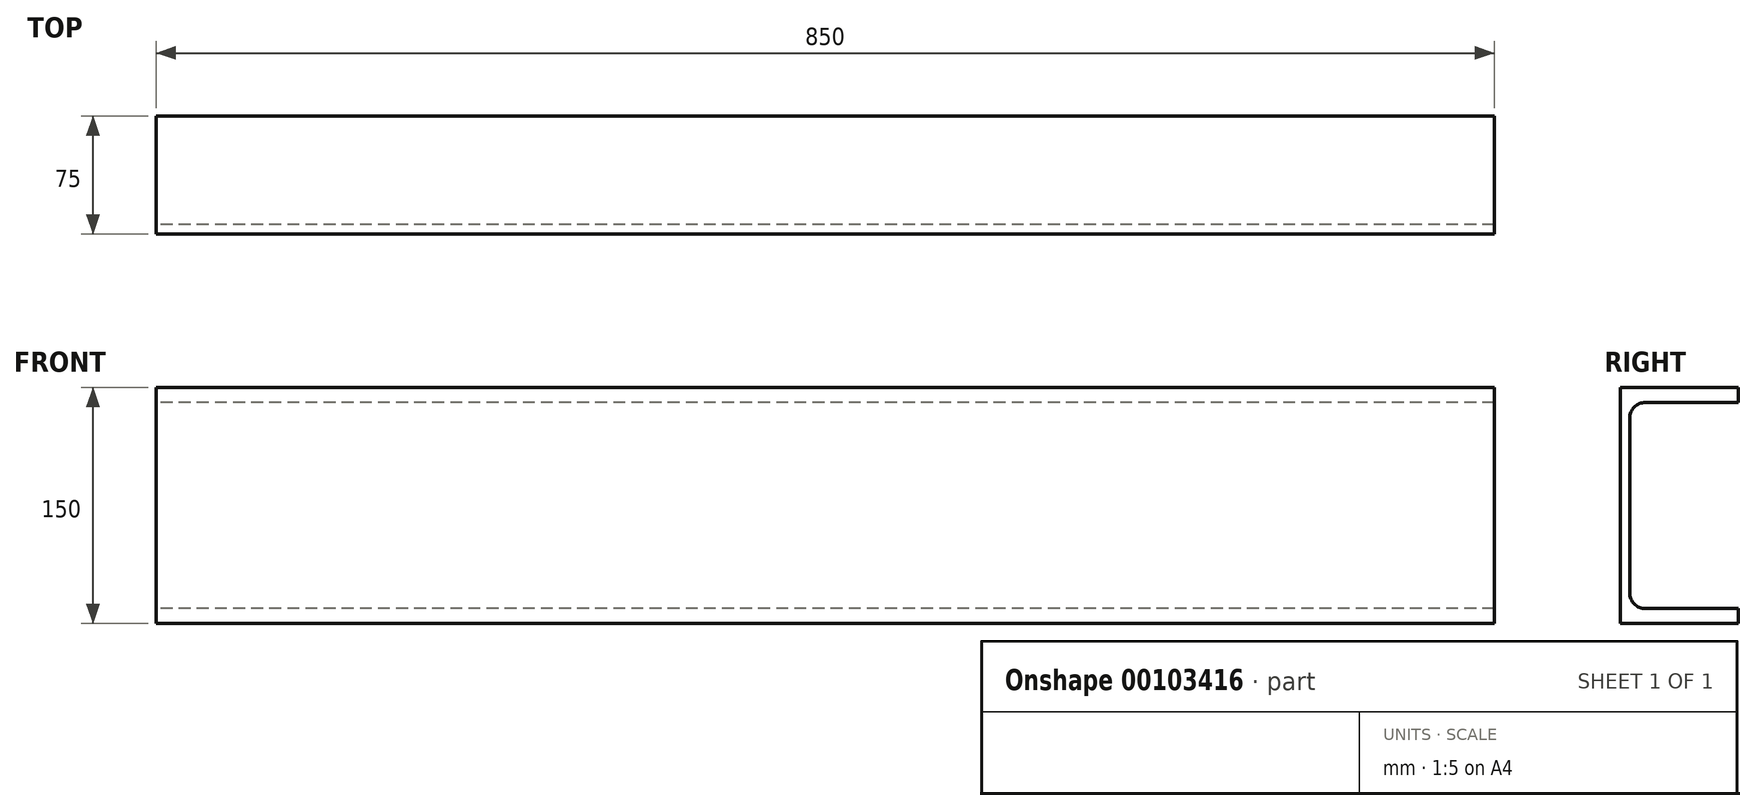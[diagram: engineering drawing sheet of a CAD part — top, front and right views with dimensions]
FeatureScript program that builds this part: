
annotation { "Feature Type Name" : "Feature", "Feature Type Description" : "" }
export const myFeature = defineFeature(function(context is Context, id is Id, definition is map)
    precondition{}
    {
        {
            var Q0;
            Q0=qCreatedBy(makeId("Right.planeOp"),FACE);
            var sketch = newSketch(context, id + "F0", { "sketchPlane" : qUnion([Q0])});
            skLineSegment(sketch, "E0", {"start": v(75, 0) * mm, "end": v(0, 0) * mm});
            skLineSegment(sketch, "E1", {"start": v(0, 0) * mm, "end": v(0, -150) * mm});
            skLineSegment(sketch, "E2", {"start": v(0, -150) * mm, "end": v(75, -150) * mm});
            skLineSegment(sketch, "E3", {"start": v(75, -150) * mm, "end": v(75, -140.5) * mm});
            skLineSegment(sketch, "E4", {"start": v(75, -140.5) * mm, "end": v(16, -140.5) * mm});
            skLineSegment(sketch, "E5", {"start": v(75, 0) * mm, "end": v(75, -9.5) * mm});
            skLineSegment(sketch, "E6", {"start": v(75, -9.5) * mm, "end": v(16, -9.5) * mm});
            skLineSegment(sketch, "E7", {"start": v(6, -19.5) * mm, "end": v(6, -130.5) * mm});
            skPoint(sketch, "E8.visualSharp", {"position": v(6, -9.5) * mm});
            skArc(sketch, "E8.filletArc", {"start": v(16, -9.5) * mm, "mid": v(8.93, -12.43) * mm, "end": v(6, -19.5) * mm});
            skPoint(sketch, "E9.visualSharp", {"position": v(6, -140.5) * mm});
            skArc(sketch, "E9.filletArc", {"start": v(6, -130.5) * mm, "mid": v(8.93, -137.57) * mm, "end": v(16, -140.5) * mm});
            skSolve(sketch);
        }
        {
            var Q0;
            Q0=qSketchRegion(id+"F0",true);
            extrude(context, id + "F1", {"entities" : qUnion([Q0]), "endBound" : BoundingType.SYMMETRIC, "depth" : 850 * mm, "offsetDistance" : 25 * mm});
        }
    });
